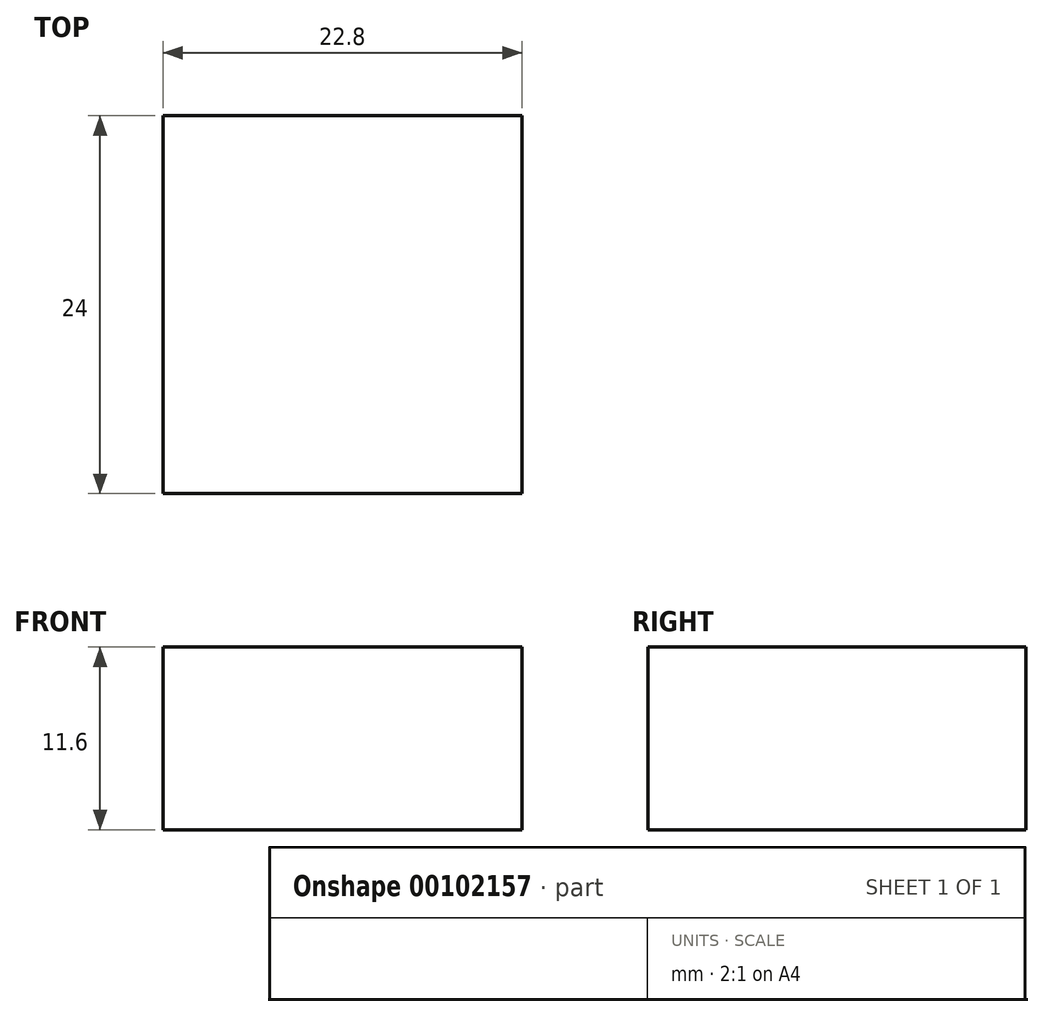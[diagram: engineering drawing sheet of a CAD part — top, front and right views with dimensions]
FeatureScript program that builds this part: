
annotation { "Feature Type Name" : "Feature", "Feature Type Description" : "" }
export const myFeature = defineFeature(function(context is Context, id is Id, definition is map)
    precondition{}
    {
        {
            var Q0;
            Q0=qCreatedBy(makeId("Front.planeOp"),FACE);
            var sketch = newSketch(context, id + "F0", { "sketchPlane" : qUnion([Q0])});
            skLineSegment(sketch, "E0.bottom", {"start": v(-63.05, 34.91) * mm, "end": v(-40.25, 34.91) * mm});
            skLineSegment(sketch, "E0.top", {"start": v(-63.05, 23.31) * mm, "end": v(-40.25, 23.31) * mm});
            skLineSegment(sketch, "E0.left", {"start": v(-63.05, 34.91) * mm, "end": v(-63.05, 23.31) * mm});
            skLineSegment(sketch, "E0.right", {"start": v(-40.25, 34.91) * mm, "end": v(-40.25, 23.31) * mm});
            skSolve(sketch);
        }
        {
            var Q0;
            Q0 = qSketchRegion(id + "F0", true);
            extrude(context, id + "F1", {"entities" : qUnion([Q0]), "depth" : 24 * mm});
        }
    });
